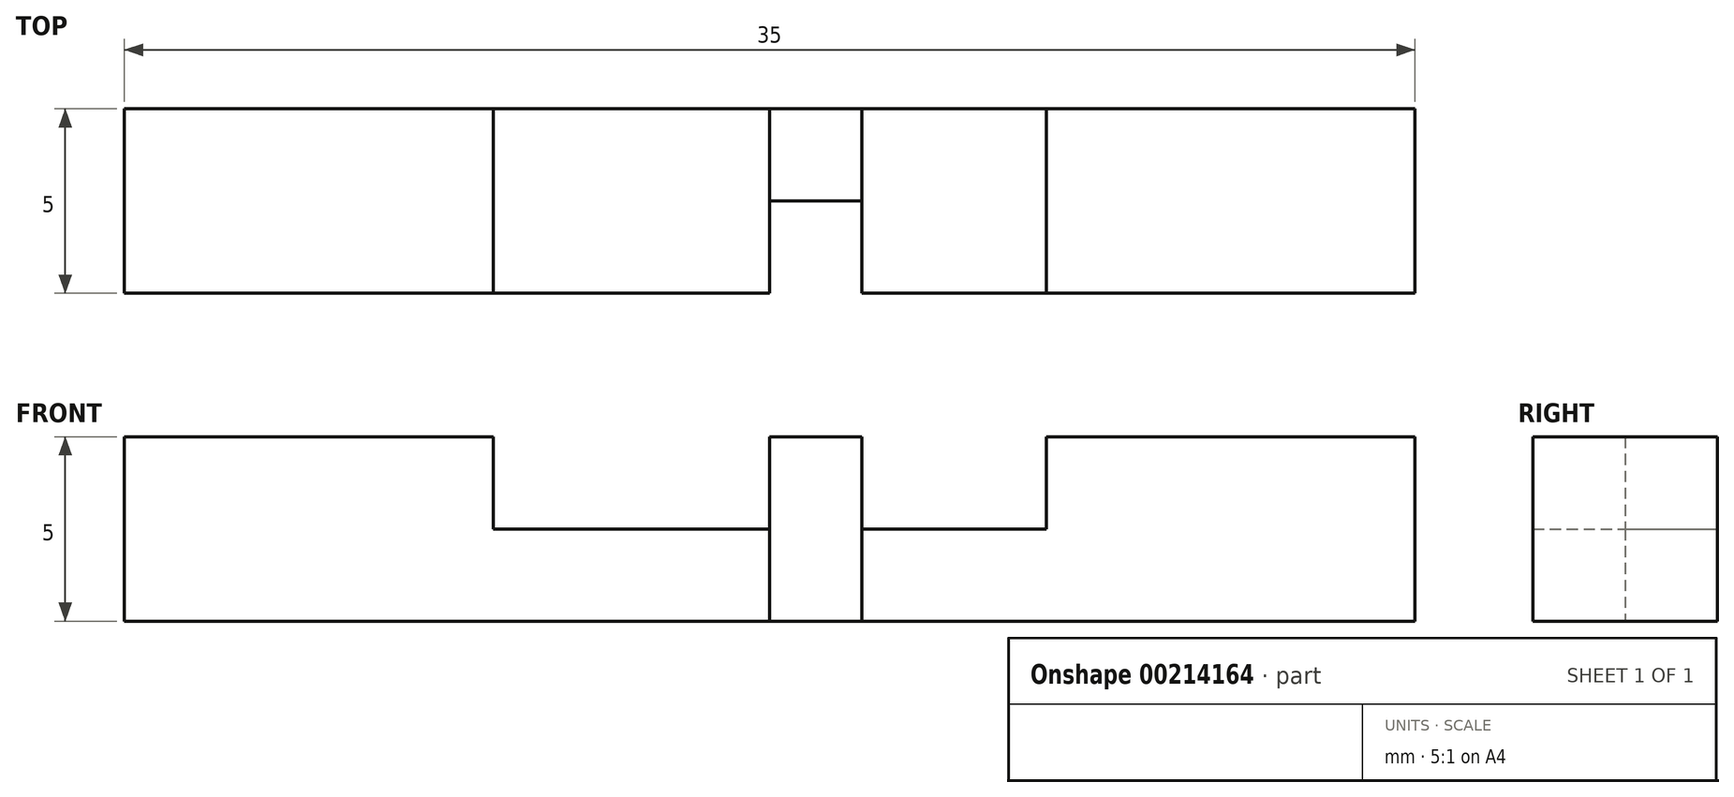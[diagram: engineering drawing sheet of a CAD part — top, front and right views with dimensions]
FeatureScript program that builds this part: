
annotation { "Feature Type Name" : "Feature", "Feature Type Description" : "" }
export const myFeature = defineFeature(function(context is Context, id is Id, definition is map)
    precondition{}
    {
        {
            var Q0;
            Q0=qCreatedBy(makeId("Top.planeOp"),FACE);
            var sketch = newSketch(context, id + "F0", { "sketchPlane" : qUnion([Q0])});
            skLineSegment(sketch, "E0.bottom", {"start": v(0, 0) * mm, "end": v(17.5, 0) * mm});
            skLineSegment(sketch, "E0.top", {"start": v(0, 5) * mm, "end": v(17.5, 5) * mm});
            skLineSegment(sketch, "E0.left", {"start": v(0, 0) * mm, "end": v(0, 5) * mm});
            skLineSegment(sketch, "E0.right", {"start": v(17.5, 0) * mm, "end": v(17.5, 5) * mm});
            skLineSegment(sketch, "E1.MirrorCS", {"start": v(0, 0) * mm, "end": v(-17.5, 0) * mm});
            skLineSegment(sketch, "E2.MirrorCS", {"start": v(0, 5) * mm, "end": v(-17.5, 5) * mm});
            skLineSegment(sketch, "E3.MirrorCS", {"start": v(-17.5, 0) * mm, "end": v(-17.5, 5) * mm});
            skSolve(sketch);
        }
        {
            var Q0;
            Q0=qSketchRegion(id+"F0",true);
            extrude(context, id + "F1", {"entities" : qUnion([Q0]), "endBound" : BoundingType.SYMMETRIC, "depth" : 5 * mm});
        }
        {
            var Q0;
            Q0=qCreatedBy(makeId("Top.planeOp"),FACE);
            var sketch = newSketch(context, id + "F2", { "sketchPlane" : qUnion([Q0])});
            skLineSegment(sketch, "E4.bottom", {"start": v(0, 0) * mm, "end": v(7.5, 0) * mm});
            skLineSegment(sketch, "E4.top", {"start": v(0, 5) * mm, "end": v(7.5, 5) * mm});
            skLineSegment(sketch, "E4.left", {"start": v(0, 0) * mm, "end": v(0, 5) * mm});
            skLineSegment(sketch, "E4.right", {"start": v(7.5, 0) * mm, "end": v(7.5, 5) * mm});
            skLineSegment(sketch, "E5.MirrorCS", {"start": v(0, 0) * mm, "end": v(-7.5, 0) * mm});
            skLineSegment(sketch, "E6.MirrorCS", {"start": v(-7.5, 0) * mm, "end": v(-7.5, 5) * mm});
            skLineSegment(sketch, "E7.MirrorCS", {"start": v(0, 5) * mm, "end": v(-7.5, 5) * mm});
            skSolve(sketch);
        }
        {
            var Q0;
            Q0=qSketchRegion(id+"F2",true);
            extrude(context, id + "F3", {"entities" : qUnion([Q0]), "operationType" : NewBodyOperationType.REMOVE, "depth" : 2.5 * mm});
        }
        {
            var Q0;
            Q0=qCreatedBy(makeId("Right.planeOp"),FACE);
            var sketch = newSketch(context, id + "F4", { "sketchPlane" : qUnion([Q0])});
            skLineSegment(sketch, "E8.bottom", {"start": v(0, 0) * mm, "end": v(2.5, 0) * mm});
            skLineSegment(sketch, "E8.top", {"start": v(0, -2.5) * mm, "end": v(2.5, -2.5) * mm});
            skLineSegment(sketch, "E8.left", {"start": v(0, 0) * mm, "end": v(0, -2.5) * mm});
            skLineSegment(sketch, "E8.right", {"start": v(2.5, 0) * mm, "end": v(2.5, -2.5) * mm});
            skSolve(sketch);
        }
        {
            var Q0;
            Q0=qSketchRegion(id+"F4",true);
            extrude(context, id + "F5", {"entities" : qUnion([Q0]), "operationType" : NewBodyOperationType.REMOVE, "depth" : 2.5 * mm});
        }
        {
            var Q0;
            Q0=qCreatedBy(makeId("Top.planeOp"),FACE);
            var sketch = newSketch(context, id + "F6", { "sketchPlane" : qUnion([Q0])});
            skLineSegment(sketch, "E9.bottom", {"start": v(0, 2.5) * mm, "end": v(2.5, 2.5) * mm});
            skLineSegment(sketch, "E9.top", {"start": v(0, 5) * mm, "end": v(2.5, 5) * mm});
            skLineSegment(sketch, "E9.left", {"start": v(0, 2.5) * mm, "end": v(0, 5) * mm});
            skLineSegment(sketch, "E9.right", {"start": v(2.5, 2.5) * mm, "end": v(2.5, 5) * mm});
            skSolve(sketch);
        }
        {
            var Q0;
            Q0 = qSketchRegion(id + "F6", true);
            extrude(context, id + "F7", {"entities" : qUnion([Q0]), "operationType" : NewBodyOperationType.ADD, "depth" : 2.5 * mm});
        }
    });
